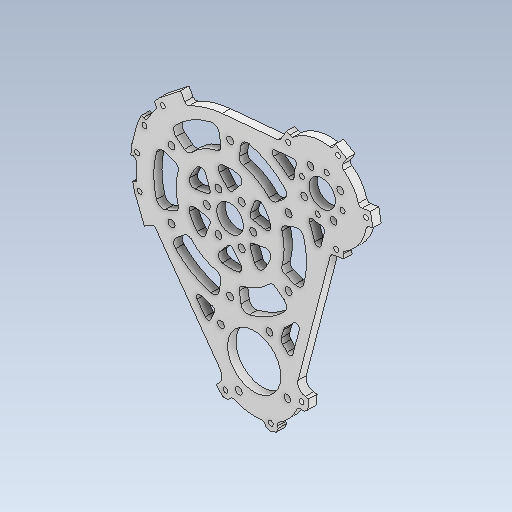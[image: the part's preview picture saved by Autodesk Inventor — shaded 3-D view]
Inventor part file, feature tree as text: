
AUTODESK INVENTOR PART (.ipt)
format: ipt  version: 2020 (Build 240168000, 168)  size: 1,395,712 bytes
history: native  units: mm
features: reference x28, sketch x13, extrude x11, fillet x11, projected_geometry x8, pattern_circular x7, other x7, shell x4, hole x2, thicken_offset x1
ambient origin geometry x8: Origin, YZ Plane, XZ Plane, XY Plane, X Axis, Y Axis, Z Axis, Center Point
bodies: Body1 (feature_tree)
feature tree (92):
  extrude  "Extrusion4"  Depth=105.0mm
  hole  "Hole2"  [1 undecoded]
  extrude  "Extrusion5"  Depth=16.0mm
  extrude  "Extrusion6"  Depth=5.0mm TaperAngle=0.0deg
  fillet  "Fillet6"  Radius=32.0mm
  fillet  "Fillet7"  Radius=5.0mm
  extrude  "Extrusion7"  Depth=6.0mm
  pattern_circular  "Circular Pattern1"  Count=3  [1 undecoded]
  extrude  "Extrusion8"  Depth=65.0mm
  pattern_circular  "Circular Pattern2"  Count=6 Angle=360.0deg
  fillet  "Fillet8"  Radius=26.0mm
  fillet  "Fillet9"  Radius=52.0mm
  pattern_circular  "Circular Pattern3"  [2 undecoded]
  fillet  "Fillet10"  Radius=10.0mm
  fillet  "Fillet11"  Radius=60.0mm
  pattern_circular  "Circular Pattern4"  [2 undecoded]
  extrude  "Extrusion9"  Depth=2.0mm
  extrude  "Extrusion10"  Depth=3.0mm TaperAngle=360.0deg
  pattern_circular  "Circular Pattern5"  [2 undecoded]
  extrude  "Extrusion11"  Depth=2.0mm TaperAngle=360.0deg
  pattern_circular  "Circular Pattern6"  [2 undecoded]
  extrude  "Extrusion12"  Depth=10.0mm TaperAngle=0.0deg
  fillet  "Fillet12"  Radius=4.2mm
  fillet  "Fillet13"  Radius=10.0mm
  fillet  "Fillet14"  Radius=60.0mm
  thicken_offset  "Thicken1"
  hole  "Hole3"  [1 undecoded]
  extrude  "Extrusion13"  TaperAngle=45.0deg  [1 undecoded]
  pattern_circular  "Circular Pattern7"  [2 undecoded]
  extrude  "Extrusion14"  Depth=10.0mm TaperAngle=0.0deg
  fillet  "Fillet15"  Radius=40.0mm
  fillet  "Fillet17"  Radius=45.0mm
  sketch  "Sketch1"  dims[d0=45.0mm d1=105.0mm]
  reference  "Reference1"
  reference  "Reference2"
  reference  "Reference3"
  reference  "Reference4"
  reference  "Reference5"
  sketch  "Sketch5"  dims[d2=50.0mm d21=5.0mm d22=0.0mm]
  reference  "Reference17"
  reference  "Reference18"
  reference  "Reference19"
  reference  "Reference20"
  reference  "Reference21"
  reference  "Reference22"
  reference  "Reference23"
  reference  "Reference24"
  reference  "Reference25"
  reference  "Reference26"
  reference  "Reference27"
  sketch  "Sketch6"  dims[d23=3.0mm d24=6.0mm d25=4.0mm d26=2.0mm d27=90.0deg d28=17.0mm d29=0.0mm d30=16.0mm]
  reference  "Reference28"
  reference  "Reference29"
  reference  "Reference30"
  sketch  "Sketch7"  dims[d31=16.0mm d32=5.0mm d33=0.0mm d34=32.0mm d35=5.0mm d36=0.0mm]
  reference  "Reference31"
  reference  "Reference32"
  reference  "Reference33"
  reference  "Reference34"
  reference  "Reference35"
  sketch  "Sketch8"  dims[d37=5.0mm d38=6.0mm d39=30.0mm]
  projected_geometry  "Projected Loop3"
  sketch  "Sketch9"  dims[d40=92.0mm d41=65.0mm]
  projected_geometry  "Projected Loop4"
  sketch  "Sketch10"  dims[d42=60.0deg]
  projected_geometry  "Projected Loop5"
  sketch  "Sketch11"  dims[d43=2.96706mm]
  projected_geometry  "Projected Loop6"
  sketch  "Sketch12"  dims[d44=1.570796mm]
  projected_geometry  "Projected Loop7"
  sketch  "Sketch13"  dims[d45=1.570796mm]
  projected_geometry  "Projected Loop8"
  sketch  "Sketch14"  dims[d46=7.330383mm]
  reference  "Reference36"
  reference  "Reference37"
  reference  "Reference38"
  reference  "Reference39"
  sketch  "Sketch15"  dims[d47=10.0mm d48=0.0mm d49=60.0mm d50=360.0deg d52=26.0mm d53=52.0mm]
  projected_geometry  "Projected Loop9"
  sketch  "Sketch16"  dims[d54=6.981317mm d55=6.981317mm d56=10.0mm d57=0.0mm d58=60.0mm d59=360.0deg d61=3.0mm d62=2.0mm d63=60.0mm d64=360.0deg d66=3.0mm d67=4.0mm d68=60.0mm d69=360.0deg d71=4.2mm d72=10.0mm d73=0.0mm d74=4.2mm d75=10.0mm d76=0.0mm d77=60.0mm d78=360.0deg d80=22.0mm d81=45.0deg d82=4.1mm d83=10.0mm d84=0.0mm d85=40.0mm d86=360.0deg d88=45.0mm d89=6.0mm d90=104.0mm d91=8.0mm d92=6.0mm d93=55.0mm d94=10.0mm d95=0.0mm d96=2.0mm d97=3.0mm d98=5.0mm d99=3.0mm d100=3.0mm d101=3.1mm d102=6.0mm d103=4.0mm d104=2.0mm d105=90.0deg d106=17.0mm d107=0.0mm d108=4.0mm d109=4.1mm d110=10.0mm d111=0.0mm d112=40.0mm d113=360.0deg d115=34.0mm d116=105.0mm d117=6.0mm d118=6.0mm d119=10.0mm d120=0.0mm d121=2.0mm d133=2.0mm d3=0.5mm d4=0.872665mm d5=0.5mm d6=0.872665mm d19=0.5mm d20=0.872665mm]
  projected_geometry  "Projected Loop10"
  parser-record x1  (decoder bookkeeping rows leaked as tree rows — omitted from the tree; the rows remain in map.json)
  other  "reducer_2.iam"
  shell  "shell_2:3"  Thickness=6.0mm
  shell  "shell_2:4"  Thickness=104.0mm
  shell  "shell_2:1"  Thickness=8.0mm
  shell  "shell_4:1"  Thickness=6.0mm
  other  "xl_wheel_ass:1"
  other  "xl_60_ori:1"
  other  "xl_60_out_2:1"
  other  "xl_20:1"
  other  "bearing_shell_1:1"
note: 14 required parameter values undecoded (feature->parameter linkage not recoverable at this tier; creation-order binding heuristic only, values carry confidence <= 0.55)
note: 1 file-system path scrubbed to <path> (originals preserved in map.json)
